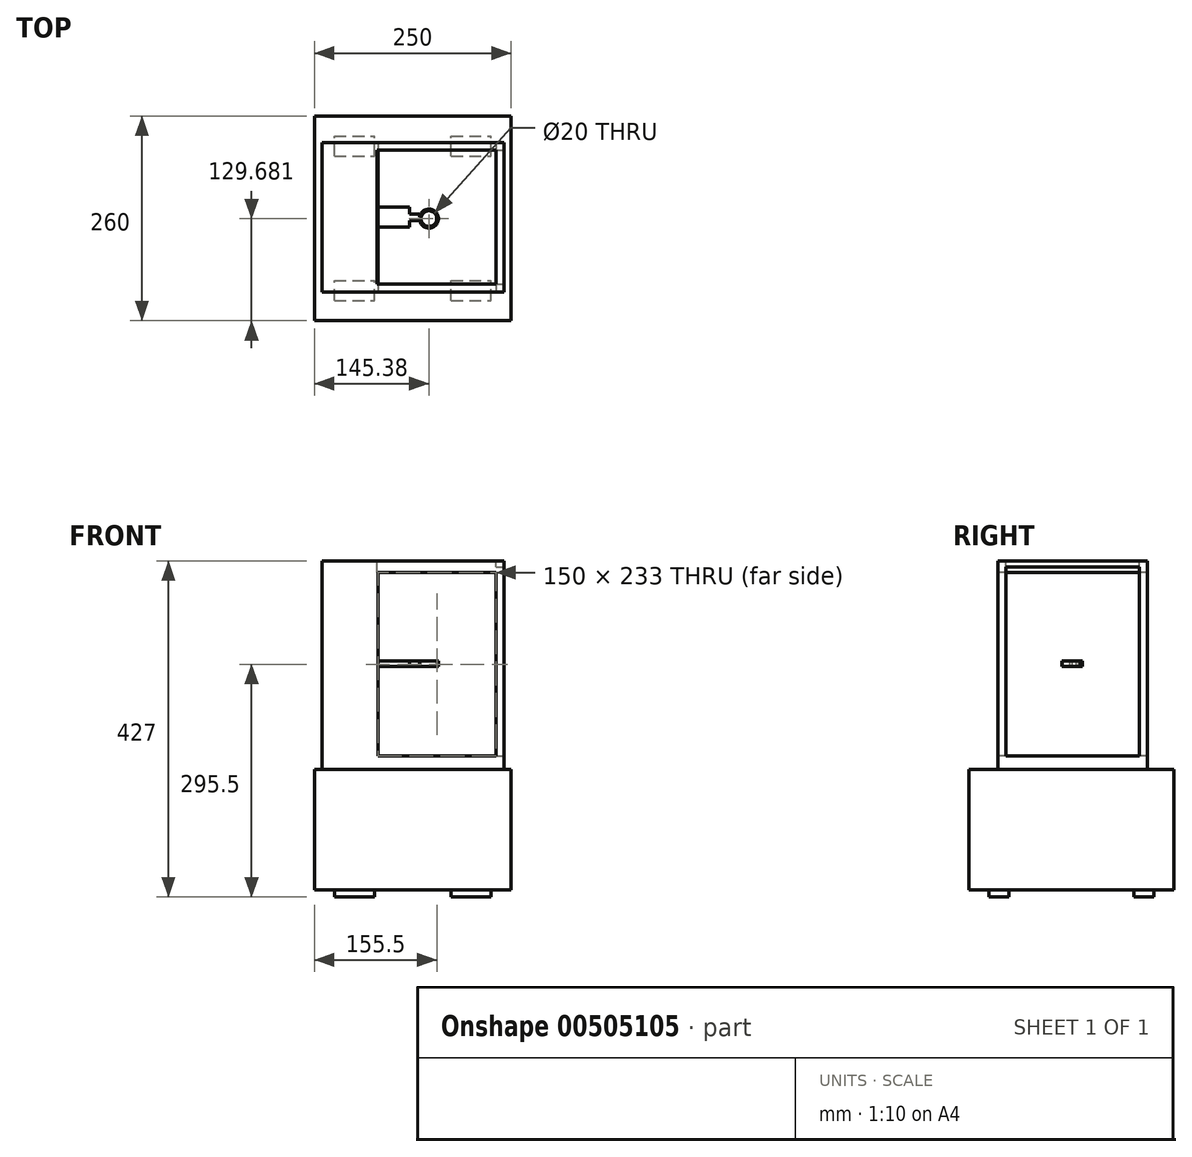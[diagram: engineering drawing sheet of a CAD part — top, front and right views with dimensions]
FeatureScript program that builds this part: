
annotation { "Feature Type Name" : "Feature", "Feature Type Description" : "" }
export const myFeature = defineFeature(function(context is Context, id is Id, definition is map)
    precondition{}
    {
        {
            var Q0;
            Q0=qCreatedBy(makeId("Front.planeOp"),FACE);
            var sketch = newSketch(context, id + "F0", { "sketchPlane" : qUnion([Q0])});
            skLineSegment(sketch, "E0.bottom", {"start": v(-125, 76.5) * mm, "end": v(125, 76.5) * mm});
            skLineSegment(sketch, "E0.top", {"start": v(-125, -76.5) * mm, "end": v(125, -76.5) * mm});
            skLineSegment(sketch, "E0.left", {"start": v(-125, 76.5) * mm, "end": v(-125, -76.5) * mm});
            skLineSegment(sketch, "E0.right", {"start": v(125, 76.5) * mm, "end": v(125, -76.5) * mm});
            skPoint(sketch, "E0.middle", {"position": v(0, 0) * mm});
            skSolve(sketch);
        }
        {
            var Q0;
            Q0 = qSketchRegion(id + "F0", true);
            extrude(context, id + "F1", {"entities" : qUnion([Q0]), "depth" : 260 * mm});
        }
        {
            var Q0;
            Q0=makeQuery(id+"F1.opExtrude","SWEPT_FACE",FACE,{"disambiguationData":[OSD([sQuery(id+"F0.wireOp",EDGE,"E0.bottom")])]});
            var sketch = newSketch(context, id + "F2", { "sketchPlane" : qUnion([Q0])});
            skLineSegment(sketch, "E1.bottom", {"start": v(-115.5, -33.47) * mm, "end": v(115.5, -33.47) * mm});
            skLineSegment(sketch, "E1.top", {"start": v(-115.5, -223.47) * mm, "end": v(115.5, -223.47) * mm});
            skLineSegment(sketch, "E1.left", {"start": v(-115.5, -33.47) * mm, "end": v(-115.5, -223.47) * mm});
            skLineSegment(sketch, "E1.right", {"start": v(115.5, -33.47) * mm, "end": v(115.5, -223.47) * mm});
            skPoint(sketch, "E1.middle", {"position": v(0, -128.47) * mm});
            skSolve(sketch);
        }
        {
            var Q0;
            Q0=makeQuery(id+"F2.imprint","IMPRINT",FACE,{"disambiguationData":[TD([[makeQuery(id+"F2.imprint","IMPRINT",EDGE,{"derivedFrom":sQuery(id+"F2.wireOp",EDGE,"E1.bottom")}),-1.0]])]});
            var Q1;
            Q1 = qSketchRegion(id + "F2", true);
            extrude(context, id + "F3", {"entities" : qUnion([Q0, Q1]), "operationType" : NewBodyOperationType.ADD, "depth" : 265 * mm});
        }
        {
            var Q0;
            Q0=makeQuery(id+"F3.opExtrude","SWEPT_FACE",FACE,{"disambiguationData":[OSD([sQuery(id+"F2.wireOp",EDGE,"E1.top")])]});
            var sketch = newSketch(context, id + "F4", { "sketchPlane" : qUnion([Q0])});
            skLineSegment(sketch, "E2.bottom", {"start": v(-44.5, 326.5) * mm, "end": v(105.5, 326.5) * mm});
            skLineSegment(sketch, "E2.top", {"start": v(-44.5, 93.5) * mm, "end": v(105.5, 93.5) * mm});
            skLineSegment(sketch, "E2.left", {"start": v(-44.5, 326.5) * mm, "end": v(-44.5, 93.5) * mm});
            skLineSegment(sketch, "E2.right", {"start": v(105.5, 326.5) * mm, "end": v(105.5, 93.5) * mm});
            skSolve(sketch);
        }
        {
            var Q0;
            Q0 = qSketchRegion(id + "F4", true);
            extrude(context, id + "F5", {"entities" : qUnion([Q0]), "operationType" : NewBodyOperationType.REMOVE, "oppositeDirection" : true, "depth" : 190 * mm});
        }
        {
            var Q0;
            Q0=makeQuery(id+"F3.opExtrude","SWEPT_FACE",FACE,{"disambiguationData":[OSD([sQuery(id+"F2.wireOp",EDGE,"E1.right")])]});
            var sketch = newSketch(context, id + "F6", { "sketchPlane" : qUnion([Q0])});
            skLineSegment(sketch, "E3.bottom", {"start": v(-213.47, 333.5) * mm, "end": v(-43.47, 333.5) * mm});
            skLineSegment(sketch, "E3.top", {"start": v(-213.47, 93.5) * mm, "end": v(-43.47, 93.5) * mm});
            skLineSegment(sketch, "E3.left", {"start": v(-213.47, 333.5) * mm, "end": v(-213.47, 93.5) * mm});
            skLineSegment(sketch, "E3.right", {"start": v(-43.47, 333.5) * mm, "end": v(-43.47, 93.5) * mm});
            skPoint(sketch, "E4.endSnap0", {"position": v(-128.47, 93.5) * mm});
            skSolve(sketch);
        }
        {
            var Q0;
            Q0=makeQuery(id+"F6.imprint","IMPRINT",FACE,{"disambiguationData":[TD([[makeQuery(id+"F6.imprint","IMPRINT",EDGE,{"derivedFrom":sQuery(id+"F6.wireOp",EDGE,"E3.bottom")}),-1.0]])]});
            extrude(context, id + "F7", {"entities" : qUnion([Q0]), "operationType" : NewBodyOperationType.REMOVE, "oppositeDirection" : true, "depth" : 10 * mm});
        }
        {
            var Q0;
            Q0=makeQuery(id+"F3.opExtrude","CAP_FACE",FACE,{"disambiguationData":[OSD([sQuery(id+"F2.wireOp",EDGE,"E1.bottom"),sQuery(id+"F2.wireOp",EDGE,"E1.top"),sQuery(id+"F2.wireOp",EDGE,"E1.left"),sQuery(id+"F2.wireOp",EDGE,"E1.right")])],"isStart":false});
            var sketch = newSketch(context, id + "F8", { "sketchPlane" : qUnion([Q0])});
            skLineSegment(sketch, "E5.bottom", {"start": v(-45.5, -43.47) * mm, "end": v(105.5, -43.47) * mm});
            skLineSegment(sketch, "E5.top", {"start": v(-45.5, -213.47) * mm, "end": v(105.5, -213.47) * mm});
            skLineSegment(sketch, "E5.left", {"start": v(-45.5, -43.47) * mm, "end": v(-45.5, -213.47) * mm});
            skLineSegment(sketch, "E5.right", {"start": v(105.5, -43.47) * mm, "end": v(105.5, -213.47) * mm});
            skPoint(sketch, "E6.endSnap0", {"position": v(105.5, -128.47) * mm});
            skSolve(sketch);
        }
        {
            var Q0;
            Q0=makeQuery(id+"F8.imprint","IMPRINT",FACE,{"disambiguationData":[TD([[makeQuery(id+"F8.imprint","IMPRINT",EDGE,{"derivedFrom":sQuery(id+"F8.wireOp",EDGE,"E5.bottom")}),-1.0]])]});
            extrude(context, id + "F9", {"entities" : qUnion([Q0]), "operationType" : NewBodyOperationType.REMOVE, "oppositeDirection" : true, "depth" : 15 * mm});
        }
        {
            var Q0;
            Q0=makeQuery(id+"F5.boolean.opBoolean","COPY",FACE,{"derivedFrom":makeQuery(id+"F5.opExtrude","SWEPT_FACE",FACE,{"disambiguationData":[OSD([sQuery(id+"F4.wireOp",EDGE,"E2.left")])]})});
            var sketch = newSketch(context, id + "F10", { "sketchPlane" : qUnion([Q0])});
            skLineSegment(sketch, "E7.bottom", {"start": v(-140.87, 214.55) * mm, "end": v(-115.87, 214.55) * mm});
            skLineSegment(sketch, "E7.top", {"start": v(-140.87, 207.55) * mm, "end": v(-115.87, 207.55) * mm});
            skLineSegment(sketch, "E7.left", {"start": v(-140.87, 214.55) * mm, "end": v(-140.87, 207.55) * mm});
            skLineSegment(sketch, "E7.right", {"start": v(-115.87, 214.55) * mm, "end": v(-115.87, 207.55) * mm});
            skPoint(sketch, "E8.endSnap0", {"position": v(-223.47, 210) * mm});
            skSolve(sketch);
        }
        {
            var Q0;
            Q0 = qSketchRegion(id + "F10", true);
            extrude(context, id + "F11", {"entities" : qUnion([Q0]), "operationType" : NewBodyOperationType.ADD, "depth" : 40 * mm});
        }
        {
            var Q0;
            Q0=makeQuery(id+"F11.opExtrude","CAP_FACE",FACE,{"disambiguationData":[OSD([sQuery(id+"F10.wireOp",EDGE,"E7.bottom"),sQuery(id+"F10.wireOp",EDGE,"E7.top"),sQuery(id+"F10.wireOp",EDGE,"E7.left"),sQuery(id+"F10.wireOp",EDGE,"E7.right")])],"isStart":false});
            var sketch = newSketch(context, id + "F12", { "sketchPlane" : qUnion([Q0])});
            skLineSegment(sketch, "E9.bottom", {"start": v(-132.63, 214.55) * mm, "end": v(-124.63, 214.55) * mm});
            skLineSegment(sketch, "E9.top", {"start": v(-132.63, 207.55) * mm, "end": v(-124.63, 207.55) * mm});
            skLineSegment(sketch, "E9.left", {"start": v(-132.63, 214.55) * mm, "end": v(-132.63, 207.55) * mm});
            skLineSegment(sketch, "E9.right", {"start": v(-124.63, 214.55) * mm, "end": v(-124.63, 207.55) * mm});
            skSolve(sketch);
        }
        {
            var Q0;
            Q0=makeQuery(id+"F12.imprint","IMPRINT",FACE,{"disambiguationData":[TD([[makeQuery(id+"F12.imprint","IMPRINT",EDGE,{"derivedFrom":sQuery(id+"F12.wireOp",EDGE,"E9.bottom")}),-1.0]])]});
            extrude(context, id + "F13", {"entities" : qUnion([Q0]), "operationType" : NewBodyOperationType.ADD, "depth" : 13 * mm});
        }
        {
            var Q0;
            Q0=makeQuery(id+"F13.boolean.opBoolean","MERGE",FACE,{"derivedFrom":[makeQuery(id+"F11.opExtrude","SWEPT_FACE",FACE,{"disambiguationData":[OSD([sQuery(id+"F10.wireOp",EDGE,"E7.bottom")])]}),makeQuery(id+"F13.opExtrude","SWEPT_FACE",FACE,{"disambiguationData":[OSD([sQuery(id+"F12.wireOp",EDGE,"E9.bottom")])]})]});
            var sketch = newSketch(context, id + "F14", { "sketchPlane" : qUnion([Q0])});
            skCircle(sketch, "E10", {"center": v(20.38, -130.32) * mm, "radius": 12 * mm});
            skPoint(sketch, "E10.first.point", {"position": v(8.5, -128.63) * mm});
            skPoint(sketch, "E10.second.point", {"position": v(32.16, -132.63) * mm});
            skPoint(sketch, "E10.third.point", {"position": v(28.66, -121.64) * mm});
            skSolve(sketch);
        }
        {
            var Q0;
            Q0 = qSketchRegion(id + "F14", true);
            extrude(context, id + "F15", {"entities" : qUnion([Q0]), "operationType" : NewBodyOperationType.ADD, "oppositeDirection" : true, "depth" : 7 * mm});
        }
        {
            var Q0;
            Q0=makeQuery(id+"F15.boolean.opBoolean","MERGE",FACE,{"derivedFrom":[makeQuery(id+"F13.boolean.opBoolean","MERGE",FACE,{"derivedFrom":[makeQuery(id+"F11.opExtrude","SWEPT_FACE",FACE,{"disambiguationData":[OSD([sQuery(id+"F10.wireOp",EDGE,"E7.bottom")])]}),makeQuery(id+"F13.opExtrude","SWEPT_FACE",FACE,{"disambiguationData":[OSD([sQuery(id+"F12.wireOp",EDGE,"E9.bottom")])]})]}),makeQuery(id+"F15.opExtrude","CAP_FACE",FACE,{"disambiguationData":[OSD([sQuery(id+"F14.wireOp",EDGE,"E10")])],"isStart":true})]});
            var sketch = newSketch(context, id + "F16", { "sketchPlane" : qUnion([Q0])});
            skCircle(sketch, "E11", {"center": v(20.38, -130.32) * mm, "radius": 10 * mm});
            skSolve(sketch);
        }
        {
            var Q0;
            Q0 = qSketchRegion(id + "F16", true);
            extrude(context, id + "F17", {"entities" : qUnion([Q0]), "operationType" : NewBodyOperationType.REMOVE, "oppositeDirection" : true, "depth" : 7 * mm});
        }
        {
            var Q0;
            Q0=makeQuery(id+"F1.opExtrude","SWEPT_FACE",FACE,{"disambiguationData":[OSD([sQuery(id+"F0.wireOp",EDGE,"E0.top")])]});
            var sketch = newSketch(context, id + "F18", { "sketchPlane" : qUnion([Q0])});
            skLineSegment(sketch, "E12.bottom", {"start": v(-99.6, 234.6) * mm, "end": v(-48.8, 234.6) * mm});
            skLineSegment(sketch, "E12.top", {"start": v(-99.6, 209.2) * mm, "end": v(-48.8, 209.2) * mm});
            skLineSegment(sketch, "E12.left", {"start": v(-99.6, 234.6) * mm, "end": v(-99.6, 209.2) * mm});
            skLineSegment(sketch, "E12.right", {"start": v(-48.8, 234.6) * mm, "end": v(-48.8, 209.2) * mm});
            skSolve(sketch);
        }
        {
            var Q0;
            Q0 = qSketchRegion(id + "F18", true);
            extrude(context, id + "F19", {"entities" : qUnion([Q0]), "operationType" : NewBodyOperationType.ADD, "depth" : 9 * mm});
        }
        {
            var Q0;
            Q0=makeQuery(id+"F1.opExtrude","SWEPT_FACE",FACE,{"disambiguationData":[OSD([sQuery(id+"F0.wireOp",EDGE,"E0.top")])]});
            var sketch = newSketch(context, id + "F20", { "sketchPlane" : qUnion([Q0])});
            skLineSegment(sketch, "E13.bottom", {"start": v(48.8, 234.6) * mm, "end": v(99.6, 234.6) * mm});
            skLineSegment(sketch, "E13.top", {"start": v(48.8, 209.2) * mm, "end": v(99.6, 209.2) * mm});
            skLineSegment(sketch, "E13.left", {"start": v(48.8, 234.6) * mm, "end": v(48.8, 209.2) * mm});
            skLineSegment(sketch, "E13.right", {"start": v(99.6, 234.6) * mm, "end": v(99.6, 209.2) * mm});
            skSolve(sketch);
        }
        {
            var Q0;
            Q0 = qSketchRegion(id + "F20", true);
            extrude(context, id + "F21", {"entities" : qUnion([Q0]), "operationType" : NewBodyOperationType.ADD, "depth" : 9 * mm});
        }
        {
            var Q0;
            Q0=makeQuery(id+"F1.opExtrude","SWEPT_FACE",FACE,{"disambiguationData":[OSD([sQuery(id+"F0.wireOp",EDGE,"E0.top")])]});
            var sketch = newSketch(context, id + "F22", { "sketchPlane" : qUnion([Q0])});
            skLineSegment(sketch, "E14.bottom", {"start": v(48.8, 50.8) * mm, "end": v(99.6, 50.8) * mm});
            skLineSegment(sketch, "E14.top", {"start": v(48.8, 25.4) * mm, "end": v(99.6, 25.4) * mm});
            skLineSegment(sketch, "E14.left", {"start": v(48.8, 50.8) * mm, "end": v(48.8, 25.4) * mm});
            skLineSegment(sketch, "E14.right", {"start": v(99.6, 50.8) * mm, "end": v(99.6, 25.4) * mm});
            skSolve(sketch);
        }
        {
            var Q0;
            Q0=makeQuery(id+"F22.imprint","IMPRINT",FACE,{"disambiguationData":[TD([[makeQuery(id+"F22.imprint","IMPRINT",EDGE,{"derivedFrom":sQuery(id+"F22.wireOp",EDGE,"E14.bottom")}),-1.0]])]});
            extrude(context, id + "F23", {"entities" : qUnion([Q0]), "operationType" : NewBodyOperationType.ADD, "depth" : 9 * mm});
        }
        {
            var Q0;
            Q0=makeQuery(id+"F1.opExtrude","SWEPT_FACE",FACE,{"disambiguationData":[OSD([sQuery(id+"F0.wireOp",EDGE,"E0.top")])]});
            var sketch = newSketch(context, id + "F24", { "sketchPlane" : qUnion([Q0])});
            skLineSegment(sketch, "E15.bottom", {"start": v(-99.6, 50.8) * mm, "end": v(-48.8, 50.8) * mm});
            skLineSegment(sketch, "E15.top", {"start": v(-99.6, 25.4) * mm, "end": v(-48.8, 25.4) * mm});
            skLineSegment(sketch, "E15.left", {"start": v(-99.6, 50.8) * mm, "end": v(-99.6, 25.4) * mm});
            skLineSegment(sketch, "E15.right", {"start": v(-48.8, 50.8) * mm, "end": v(-48.8, 25.4) * mm});
            skSolve(sketch);
        }
        {
            var Q0;
            Q0=makeQuery(id+"F24.imprint","IMPRINT",FACE,{"disambiguationData":[TD([[makeQuery(id+"F24.imprint","IMPRINT",EDGE,{"derivedFrom":sQuery(id+"F24.wireOp",EDGE,"E15.bottom")}),-1.0]])]});
            extrude(context, id + "F25", {"entities" : qUnion([Q0]), "operationType" : NewBodyOperationType.ADD, "depth" : 9 * mm});
        }
    });
